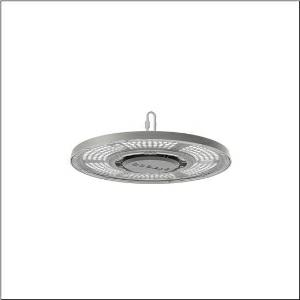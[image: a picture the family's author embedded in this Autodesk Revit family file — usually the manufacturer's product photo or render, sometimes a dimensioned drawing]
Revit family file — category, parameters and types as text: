
# Revit family: highbay_31-s_51hc417a4fmb
name_source: partatom
category: Lighting Fixtures
units: mm (PartAtom-declared; Revit-internal decimal feet)

## family parameters
Cut with Voids When Loaded = No
Host = Face
Light Source = No
Part Type = Normal
Room Calculation Point = No
Round Connector Dimension = Use Diameter
Shared = No

## types (1)
- Highbay 31-S (1 x LED, 14000 lm, 94 W, 4000K)
    Apparent Load = 94 VA
    CIE Flux Codes = 94 98 100 100 100
    Color Rendering = 80
    Color Temperature = 4000K
    Default Elevation = 1800 mm
    Description = Highbay 31-S, LED high bay luminaire, primary light control with lens, of PC, primary optical cover: cover panel, of PC, transparent, light emission: direct distribution, primary light characteristic: rotationally symmetric, installation type: suspended mounting, surface-mounted, LED, rated luminous flux: 14.000lm, luminous efficacy: 150lm/W, light colour: 840, colour temperature: 4000K, control gear: ECG, with cable, 3x 1.0mm², free wire ends, mains connection: 220..240V, AC/DC, 0/50..60Hz, cable length: 1,5m, rated input power: 94W, housing, rotationally symmetric, of diecast aluminium, grey aluminium (RAL 9007), diameter: 339mm, protection rating (complete): IP65, insulation class (complete): insulation class I (protective earthing), certification: CE, ENEC, UKCA, protection symbol: D, impact resistance: IK08, permissible operating ambient temperature: -30..+45°C, standard: EN 60598-2-22, EN 60598, corresponds to IFS (International Featured Standards) requirements for safety and quality in the food industry, packaging unit: 1 piece
    Height = 141 mm
    Lamp = 1 x LED
    Lamp Light Flux = 14000 lm
    Lamp Power = 94 W
    Lamp count = 1
    Length = 339 mm
    Luminous efficacy = 149 lm/W
    Manufacturer = Siteco
    ModVariant = No
    Model = 51HC417A4FMB
    Mounting Place = Ceiling
    Mounting Type = Pendant
    Number of Poles = 1
    OnlyDefault = Yes
    Power Factor = 1
    Product Name = Highbay 31-S
    Product group = LED high bay luminaire
    ProductGroupID = 903
    Protection Class = Protection class I
    Protection Degree = IP 65
    RLX_Detail_Level = 1
    RlxData = <blob elided: 106889 chars, md5=f456ed9e>
    Socket = socket
    Standby Power = 0 W
    System Light Flux = 14000 lm
    System Power = 94 W
    Type Comments = Product without accessories
    Type Image = l_1007237.jpg
    URL = http://relux.com
    VarID = ---
    Voltage = 0 V
    Weight = 0.00 kg
    Width = 0 mm  [stored 0 ft]

note: [stored X ft] marks values corroborated as IEEE doubles in the binary element streams (Revit-internal decimal feet)

## geometry (parser evidence)
native form markers: Blend x4, Sweep x10
no freeform markers — native parametric forms only
